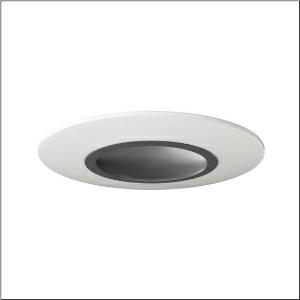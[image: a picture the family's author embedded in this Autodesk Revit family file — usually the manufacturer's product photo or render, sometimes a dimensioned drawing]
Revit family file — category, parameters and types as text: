
# Revit family: rondel_21_0md5307l1840
name_source: partatom
category: Lighting Fixtures
units: mm (PartAtom-declared; Revit-internal decimal feet)

## family parameters
Cut with Voids When Loaded = No
Host = Face
Light Source = No
Part Type = Normal
Room Calculation Point = No
Round Connector Dimension = Use Diameter
Shared = No

## types (1)
- Rondel 21 (1 x LED 4000K / CRI = 80 (unbekannt), 1800 lm, 4000K)
    Apparent Load = 18 VA
    CIE Flux Codes = 43 74 92 91 100
    Color Rendering = 80
    Color Temperature = 4000K
    Default Elevation = 1800 mm  [stored 5.90551 ft]
    Description = Rondel 21, wall and ceiling luminaire, of PC, opal, light emission: direct distribution, installation type: surface-mounted, LED, rated luminous flux: 1.800lm, luminous efficacy: 100lm/W, light colour: 840, colour temperature: 4000K, control gear: ECG, with terminal, 2-pole, mains connection: 220..240V, AC, 50/60Hz, rated input power: 18W, housing, round, of sheet steel, powder-coated, white, diameter: 380mm, height: 28mm, cover, of PC, graphite (RAL 7037), protection rating (complete): IP40, insulation class (complete): insulation class II (safety insulation), certification: CE, impact resistance: IK03, permissible operating ambient temperature: -20..+40°C, permissible storage temperature: -20..+80°C, packaging unit: 1 piece
    Height = 28 mm
    Lamp = 1 x LED 4000K / CRI >= 80 (unbekannt)
    Lamp Light Flux = 1800 lm
    Lamp count = 1
    Length = 380 mm
    Luminous efficacy = 100 lm/W
    Manufacturer = Siteco
    ModVariant = No
    Model = 0MD5307L1840
    Mounting Place = Ceiling
    Mounting Type = Surface mounted
    Number of Poles = 1
    OnlyDefault = Yes
    Power Factor = 1
    Product Name = Rondel 21
    Product group = wall and ceiling luminaire
    ProductGroupID = 301
    Protection Class = Protection class II
    Protection Degree = IP 40
    RLX_Detail_Level = 1
    RLX_Emergency_Light_Flux = 0 lm
    RLX_Emergency_Type = 0
    RLX_Emergency_Type_DB = No
    RlxData = <blob elided: 61673 chars, md5=ca9ca3be>
    Socket = socket
    Standby Power = 0 W
    System Light Flux = 1800 lm
    System Power = 18 W
    Type Comments = Product without accessories
    Type Image = l_1005688.jpg
    URL = http://relux.com
    VarID = ---
    Voltage = 0 V
    Weight = 0.00 kg
    Width = 0 mm  [stored 0 ft]

note: [stored X ft] marks values corroborated as IEEE doubles in the binary element streams (Revit-internal decimal feet)

## geometry (parser evidence)
native form markers: Blend x4, Sweep x13
no freeform markers — native parametric forms only
